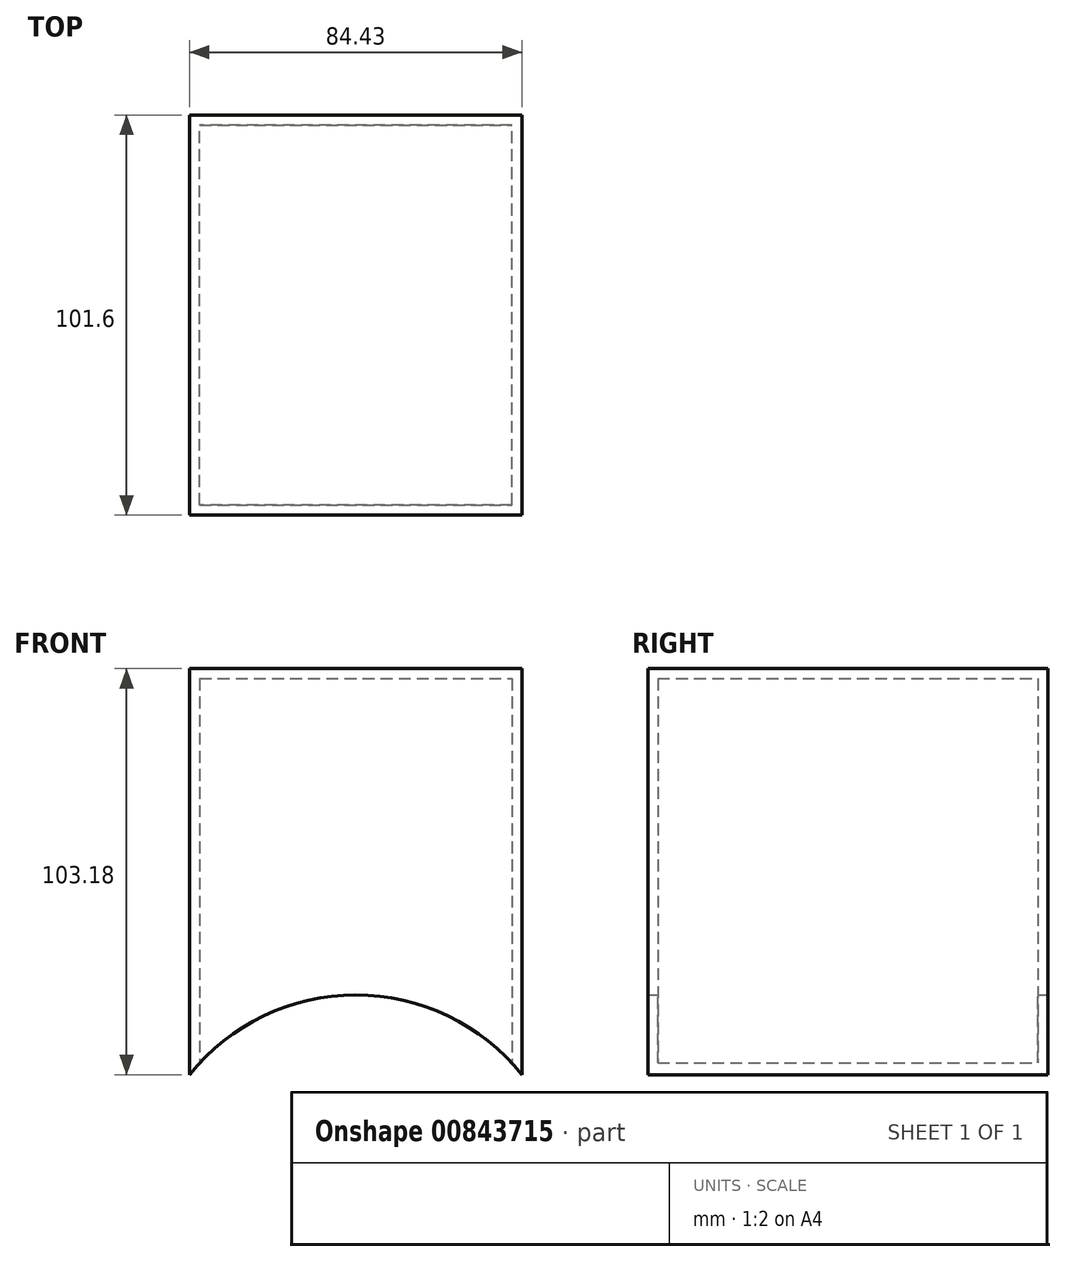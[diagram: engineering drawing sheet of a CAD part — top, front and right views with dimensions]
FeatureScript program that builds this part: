
annotation { "Feature Type Name" : "Feature", "Feature Type Description" : "" }
export const myFeature = defineFeature(function(context is Context, id is Id, definition is map)
    precondition{}
    {
        {
            var Q0;
            Q0=qCreatedBy(makeId("Front.planeOp"),FACE);
            var sketch = newSketch(context, id + "F0", { "sketchPlane" : qUnion([Q0])});
            skLineSegment(sketch, "E0.bottom", {"start": v(-44.7, 49.52) * mm, "end": v(39.73, 49.52) * mm});
            skLineSegment(sketch, "E0.left", {"start": v(-44.7, 49.52) * mm, "end": v(-44.7, -53.66) * mm});
            skLineSegment(sketch, "E0.right", {"start": v(39.73, 49.52) * mm, "end": v(39.73, -53.66) * mm});
            skArc(sketch, "E1", {"start": v(39.73, -53.66) * mm, "mid": v(-2.48, -33.38) * mm, "end": v(-44.7, -53.66) * mm});
            skSolve(sketch);
        }
        {
            var Q0;
            Q0 = qSketchRegion(id + "F0", true);
            extrude(context, id + "F1", {"entities" : qUnion([Q0]), "depth" : 101.6 * mm, "offsetDistance" : 25.4 * mm});
        }
        {
            var Q0;
            Q0=makeQuery(id+"F1.opExtrude","SWEPT_FACE",FACE,{"disambiguationData":[OSD([sQuery(id+"F0.wireOp",EDGE,"E1")])]});
            shell(context, id + "F2", {"entities" : qUnion([Q0]), "thickness" : 2.54 * mm});
        }
    });
